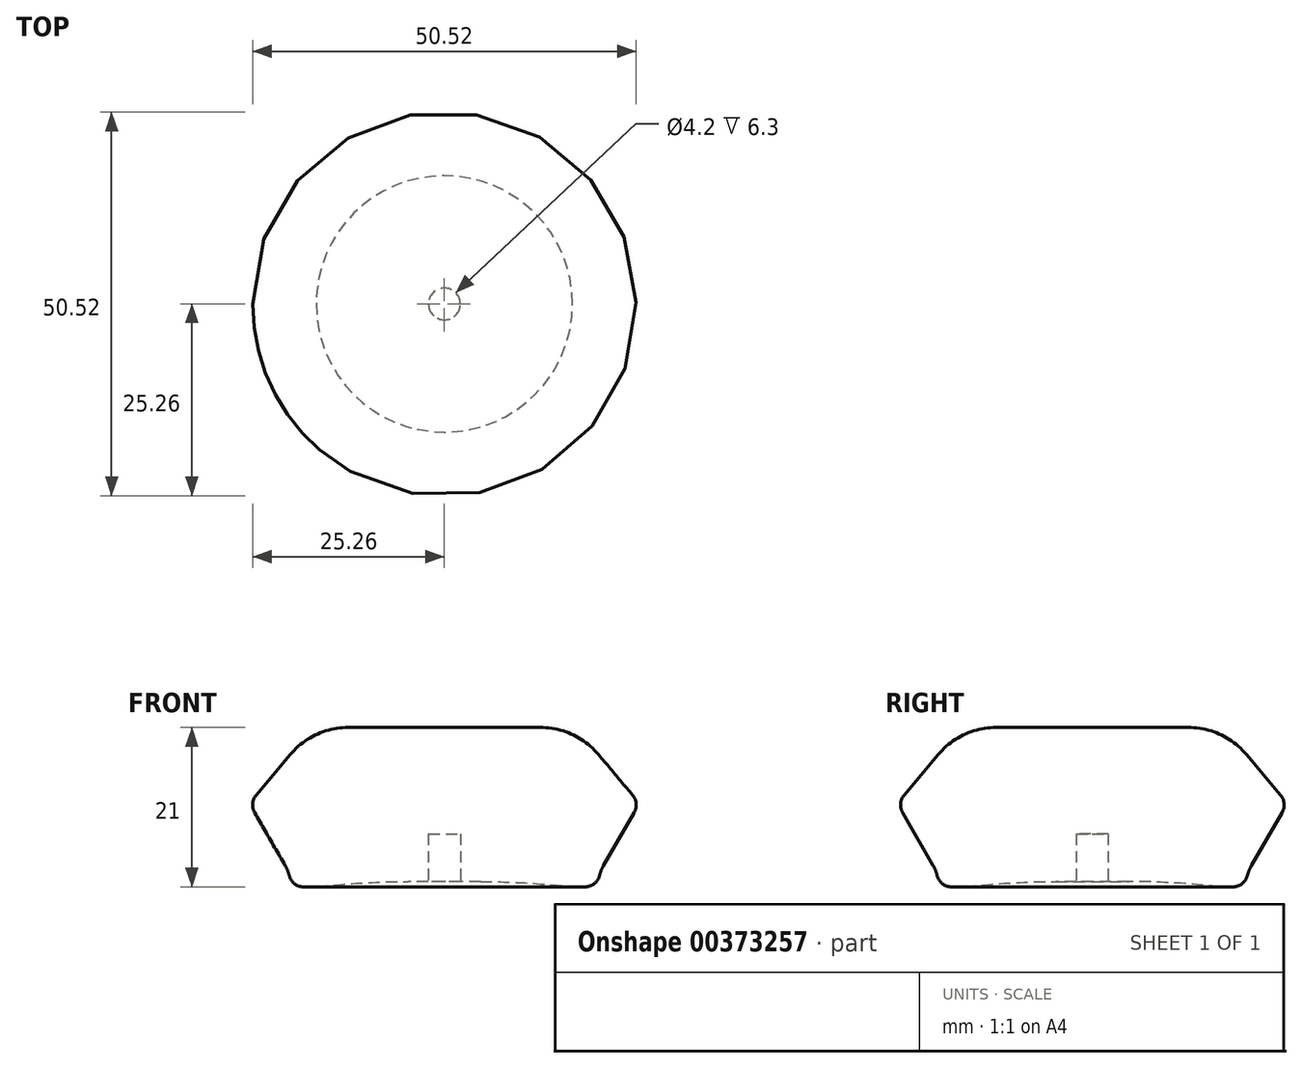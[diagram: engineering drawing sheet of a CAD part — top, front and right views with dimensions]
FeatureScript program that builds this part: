
annotation { "Feature Type Name" : "Feature", "Feature Type Description" : "" }
export const myFeature = defineFeature(function(context is Context, id is Id, definition is map)
    precondition{}
    {
        {
            var Q0;
            Q0=qCreatedBy(makeId("Top.planeOp"),FACE);
            var sketch = newSketch(context, id + "F0", { "sketchPlane" : qUnion([Q0])});
            skCircle(sketch, "E0", {"center": v(0, 0) * mm, "radius": 20.5 * mm});
            skSolve(sketch);
        }
        {
            var Q0;
            Q0=makeQuery(id+"F0.imprint","IMPRINT",FACE,{"disambiguationData":[TD([[makeQuery(id+"F0.imprint","IMPRINT",EDGE,{"derivedFrom":sQuery(id+"F0.wireOp",EDGE,"E0")}),1.0]])]});
            extrude(context, id + "F1", {"entities" : qUnion([Q0]), "depth" : 2 * mm});
        }
        {
            var Q0;
            Q0=makeQuery(id+"F1.opExtrude","CAP_FACE",FACE,{"disambiguationData":[OSD([sQuery(id+"F0.wireOp",EDGE,"E0")])],"isStart":false});
            extrude(context, id + "F2", {"entities" : qUnion([Q0]), "operationType" : NewBodyOperationType.ADD, "depth" : 9 * mm, "hasDraft" : true, "draftAngle" : 30 * degree});
        }
        {
            var Q0;
            Q0=makeQuery(id+"F2.opExtrude","CAP_FACE",FACE,{"disambiguationData":[OSD([sQuery(id+"F0.wireOp",EDGE,"E0")])],"isStart":false});
            extrude(context, id + "F3", {"entities" : qUnion([Q0]), "operationType" : NewBodyOperationType.ADD, "depth" : 10 * mm, "hasDraft" : true, "draftAngle" : 40 * degree, "draftPullDirection" : true});
        }
        {
            var Q0;
            Q0=makeQuery(id+"F3.opExtrude","CAP_EDGE",EDGE,{"disambiguationData":[OSD([sQuery(id+"F0.wireOp",EDGE,"E0")])],"isStart":false});
            fillet(context, id + "F4", {"entities" : qUnion([Q0]), "radius" : 10 * mm, "tangentPropagation" : true, "allowEdgeOverflow" : false});
        }
        {
            var Q0;
            {var subQ0=sQuery(id+"F0.wireOp",EDGE,"E0");Q0=makeQuery(id+"F3.boolean.opBoolean","MERGE",EDGE,{"derivedFrom":[makeQuery(id+"F2.opExtrude","CAP_EDGE",EDGE,{"disambiguationData":[OSD([subQ0])],"isStart":false}),makeQuery(id+"F3.opExtrude","CAP_EDGE",EDGE,{"disambiguationData":[OSD([subQ0])],"isStart":true})]});}
            fillet(context, id + "F5", {"entities" : qUnion([Q0]), "radius" : 2 * mm, "tangentPropagation" : true, "allowEdgeOverflow" : false});
        }
        {
            var Q0;
            Q0=makeQuery(id+"F1.opExtrude","CAP_FACE",FACE,{"disambiguationData":[OSD([sQuery(id+"F0.wireOp",EDGE,"E0")])],"isStart":true});
            var sketch = newSketch(context, id + "F6", { "sketchPlane" : qUnion([Q0])});
            skCircle(sketch, "E1", {"center": v(0, 0) * mm, "radius": 2.1 * mm});
            skSolve(sketch);
        }
        {
            var Q0;
            Q0=makeQuery(id+"F6.imprint","IMPRINT",FACE,{"disambiguationData":[TD([[makeQuery(id+"F6.imprint","IMPRINT",EDGE,{"derivedFrom":sQuery(id+"F6.wireOp",EDGE,"E1")}),1.0]])]});
            extrude(context, id + "F7", {"entities" : qUnion([Q0]), "operationType" : NewBodyOperationType.REMOVE, "oppositeDirection" : true, "depth" : 7 * mm});
        }
        {
            var Q0;
            Q0=makeQuery(id+"F1.opExtrude","CAP_EDGE",EDGE,{"disambiguationData":[OSD([sQuery(id+"F0.wireOp",EDGE,"E0")])],"isStart":true});
            fillet(context, id + "F8", {"entities" : qUnion([Q0]), "radius" : 2 * mm, "tangentPropagation" : true, "allowEdgeOverflow" : false});
        }
        {
            var Q0;
            {var subQ0=sQuery(id+"F0.wireOp",EDGE,"E0");Q0=makeQuery(id+"F8.opFillet","BLEND_EDGE",EDGE,{"blendedFrom":[makeQuery(id+"F1.opExtrude","CAP_EDGE",EDGE,{"disambiguationData":[OSD([subQ0])],"isStart":true}),makeQuery(id+"F2.opExtrude","SWEPT_FACE",FACE,{"disambiguationData":[OSD([subQ0])]})],"blendedInto":[makeQuery(id+"F2.opExtrude","SWEPT_FACE",FACE,{"disambiguationData":[OSD([subQ0])]})]});}
            fillet(context, id + "F9", {"entities" : qUnion([Q0]), "radius" : 5 * mm, "tangentPropagation" : true, "allowEdgeOverflow" : false});
        }
        {
            var Q0;
            Q0=qCreatedBy(makeId("Top.planeOp"),FACE);
            var sketch = newSketch(context, id + "F10", { "sketchPlane" : qUnion([Q0])});
            skCircle(sketch, "E2", {"center": v(0, 0) * mm, "radius": 105 * mm});
            skSolve(sketch);
        }
        {
            var Q0;
            Q0=makeQuery(id+"F10.imprint","IMPRINT",FACE,{"disambiguationData":[TD([[makeQuery(id+"F10.imprint","IMPRINT",EDGE,{"derivedFrom":sQuery(id+"F10.wireOp",EDGE,"E2")}),1.0]])]});
            extrude(context, id + "F11", {"entities" : qUnion([Q0]), "depth" : 73.7 * mm});
        }
        {
            var Q0;
            Q0=makeQuery(id+"F11.opExtrude","CAP_EDGE",EDGE,{"disambiguationData":[OSD([sQuery(id+"F10.wireOp",EDGE,"E2")])],"isStart":false});
            fillet(context, id + "F12", {"entities" : qUnion([Q0]), "radius" : 105 * mm, "tangentPropagation" : true, "allowEdgeOverflow" : false});
        }
        {
            var Q0;
            Q0=makeQuery(id+"F11.opExtrude","SWEPT_BODY",BODY,{"disambiguationData":[OSD([sQuery(id+"F10.wireOp",EDGE,"E2")])]});
            transform(context, id + "F13", {"entities" : qUnion([Q0]), "transformType" : TransformType.TRANSLATION_3D, "dx" : 0 * mm, "dy" : 0 * mm, "dz" : -34.1 * mm, "makeCopy" : false});
        }
        {
            var Q0;
            Q0=makeQuery(id+"F11.opExtrude","SWEPT_BODY",BODY,{"disambiguationData":[OSD([sQuery(id+"F10.wireOp",EDGE,"E2")])]});
            transform(context, id + "F14", {"entities" : qUnion([Q0]), "transformType" : TransformType.TRANSLATION_3D, "dx" : 0 * mm, "dy" : 0 * mm, "dz" : -38.9 * mm, "makeCopy" : false});
        }
        {
            var Q0;
            Q0=makeQuery(id+"F11.opExtrude","SWEPT_BODY",BODY,{"disambiguationData":[OSD([sQuery(id+"F10.wireOp",EDGE,"E2")])]});
            var Q1;
            Q1=makeQuery(id+"F1.opExtrude","SWEPT_BODY",BODY,{"disambiguationData":[OSD([sQuery(id+"F0.wireOp",EDGE,"E0")])]});
            booleanBodies(context, id + "F15", {"operationType" : BooleanOperationType.SUBTRACTION, "tools" : qUnion([Q0]), "targets" : qUnion([Q1])});
        }
    });
